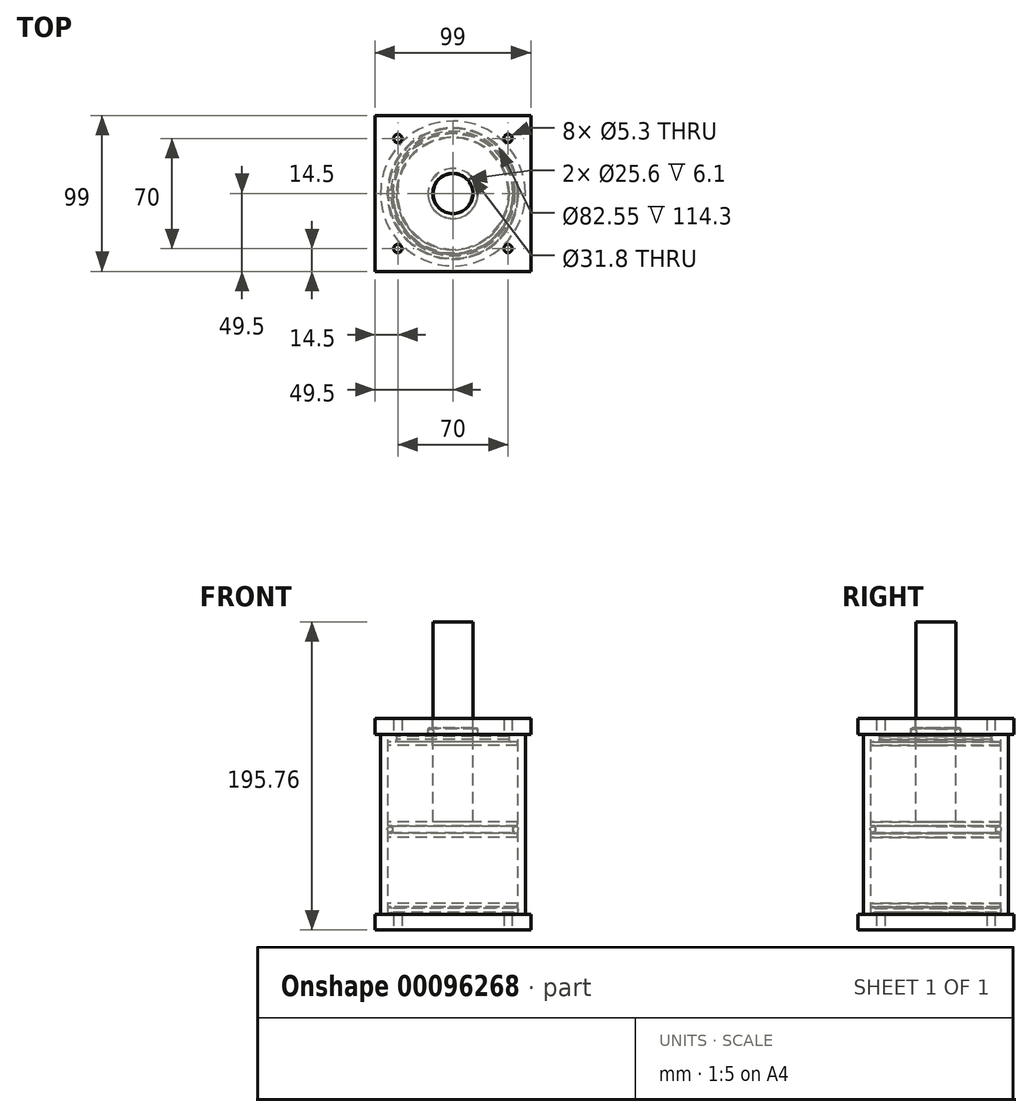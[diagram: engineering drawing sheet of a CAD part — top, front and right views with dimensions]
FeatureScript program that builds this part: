
annotation { "Feature Type Name" : "Feature", "Feature Type Description" : "" }
export const myFeature = defineFeature(function(context is Context, id is Id, definition is map)
    precondition{}
    {
        {
            var Q0;
            Q0=qCreatedBy(makeId("Front.planeOp"),FACE);
            var sketch = newSketch(context, id + "F0", { "sketchPlane" : qUnion([Q0])});
            skLineSegment(sketch, "E0", {"start": v(0, 90.15) * mm, "end": v(0, -78.3) * mm, "construction": true});
            skSolve(sketch);
        }
        {
            var Q0;
            Q0=qCreatedBy(makeId("Front.planeOp"),FACE);
            var sketch = newSketch(context, id + "F1", { "sketchPlane" : qUnion([Q0])});
            skLineSegment(sketch, "E1", {"start": v(0, 0) * mm, "end": v(12.7, 0) * mm});
            skLineSegment(sketch, "E2", {"start": v(12.7, 0) * mm, "end": v(12.7, 127) * mm});
            skLineSegment(sketch, "E3", {"start": v(12.7, 127) * mm, "end": v(0, 127) * mm});
            skLineSegment(sketch, "E4", {"start": v(0, 127) * mm, "end": v(0, 0) * mm});
            skSolve(sketch);
        }
        {
            var Q0;
            Q0=qCreatedBy(makeId("Front.planeOp"),FACE);
            var sketch = newSketch(context, id + "F2", { "sketchPlane" : qUnion([Q0])});
            skLineSegment(sketch, "E5", {"start": v(41.27, 55.54) * mm, "end": v(41.28, -58.76) * mm});
            skLineSegment(sketch, "E6", {"start": v(41.27, 55.54) * mm, "end": v(46.04, 55.54) * mm});
            skLineSegment(sketch, "E7", {"start": v(46.04, 55.54) * mm, "end": v(46.04, -58.76) * mm});
            skLineSegment(sketch, "E8", {"start": v(46.04, -58.76) * mm, "end": v(41.28, -58.76) * mm});
            skPoint(sketch, "E9.orphan", {"position": v(41.28, -58.76) * mm});
            skLineSegment(sketch, "E10", {"start": v(46.04, -1.61) * mm, "end": v(-49.68, -1.61) * mm, "construction": true});
            skSolve(sketch);
        }
        {
            var Q0;
            Q0=qCreatedBy(makeId("Front.planeOp"),FACE);
            var sketch = newSketch(context, id + "F3", { "sketchPlane" : qUnion([Q0])});
            skLineSegment(sketch, "E11", {"start": v(0, 0) * mm, "end": v(41.17, 0) * mm});
            skLineSegment(sketch, "E12", {"start": v(41.17, 0) * mm, "end": v(41.17, -2.6) * mm});
            skLineSegment(sketch, "E13", {"start": v(41.17, -2.6) * mm, "end": v(38.19, -2.6) * mm});
            skLineSegment(sketch, "E14", {"start": v(38.19, -2.6) * mm, "end": v(38.19, -7.4) * mm});
            skLineSegment(sketch, "E15", {"start": v(38.19, -7.4) * mm, "end": v(41.17, -7.4) * mm});
            skLineSegment(sketch, "E16", {"start": v(41.17, -7.4) * mm, "end": v(41.17, -10) * mm});
            skLineSegment(sketch, "E17", {"start": v(41.17, -10) * mm, "end": v(0, -10) * mm});
            skLineSegment(sketch, "E18", {"start": v(0, -10) * mm, "end": v(0, 0) * mm});
            skCircle(sketch, "E19", {"center": v(39.95, -4.9) * mm, "radius": 1.76 * mm});
            skSolve(sketch);
        }
        {
            var Q0;
            Q0=qCreatedBy(makeId("Front.planeOp"),FACE);
            var sketch = newSketch(context, id + "F4", { "sketchPlane" : qUnion([Q0])});
            skLineSegment(sketch, "E20", {"start": v(0, -51.76) * mm, "end": v(0, -68.76) * mm});
            skLineSegment(sketch, "E21", {"start": v(0, -68.76) * mm, "end": v(70, -68.76) * mm});
            skLineSegment(sketch, "E22", {"start": v(70, -68.76) * mm, "end": v(70, -58.76) * mm});
            skLineSegment(sketch, "E23", {"start": v(70, -58.76) * mm, "end": v(38.58, -58.76) * mm});
            skLineSegment(sketch, "E24", {"start": v(41.17, -53.96) * mm, "end": v(41.17, -51.76) * mm});
            skLineSegment(sketch, "E25.trimOffspring", {"start": v(41.17, -51.76) * mm, "end": v(0, -51.76) * mm});
            skCircle(sketch, "E26", {"center": v(39.92, -56.36) * mm, "radius": 1.77 * mm});
            skLineSegment(sketch, "E27", {"start": v(38.58, -58.76) * mm, "end": v(38.58, -53.96) * mm});
            skLineSegment(sketch, "E28", {"start": v(38.58, -53.96) * mm, "end": v(41.17, -53.96) * mm});
            skLineSegment(sketch, "E29.MirrorCS", {"start": v(35.85, 50.74) * mm, "end": v(41.17, 50.74) * mm});
            skLineSegment(sketch, "E30.MirrorCS", {"start": v(35.85, 55.54) * mm, "end": v(35.85, 50.74) * mm});
            skCircle(sketch, "E31.MirrorC", {"center": v(37.32, 53.26) * mm, "radius": 1.77 * mm});
            skLineSegment(sketch, "E32.MirrorCS", {"start": v(70, 65.54) * mm, "end": v(70, 55.54) * mm});
            skLineSegment(sketch, "E33.MirrorCS", {"start": v(41.17, 48.54) * mm, "end": v(12.8, 48.54) * mm});
            skLineSegment(sketch, "E34.MirrorCS", {"start": v(70, 55.54) * mm, "end": v(35.85, 55.54) * mm});
            skLineSegment(sketch, "E35.MirrorCS", {"start": v(41.17, 50.74) * mm, "end": v(41.17, 48.54) * mm});
            skLineSegment(sketch, "E36.MirrorCS", {"start": v(12.8, 65.54) * mm, "end": v(70, 65.54) * mm});
            skLineSegment(sketch, "E37", {"start": v(12.8, 48.54) * mm, "end": v(12.8, 54.64) * mm});
            skPoint(sketch, "E38", {"position": v(38.58, -56.36) * mm});
            skLineSegment(sketch, "E39", {"start": v(12.8, 54.64) * mm, "end": v(15.9, 54.64) * mm});
            skLineSegment(sketch, "E40", {"start": v(15.9, 54.64) * mm, "end": v(15.9, 59.44) * mm});
            skLineSegment(sketch, "E41", {"start": v(15.9, 59.44) * mm, "end": v(12.8, 59.44) * mm});
            skLineSegment(sketch, "E42.trimOffspring", {"start": v(12.8, 59.44) * mm, "end": v(12.8, 65.54) * mm});
            skCircle(sketch, "E43", {"center": v(14.07, 57.14) * mm, "radius": 1.76 * mm});
            skLineSegment(sketch, "E44", {"start": v(70, -58.76) * mm, "end": v(70, 76.42) * mm, "construction": true});
            skSolve(sketch);
        }
        {
            var Q0;
            Q0=makeQuery(id+"F3.imprint","IMPRINT",FACE,{"disambiguationData":[TD([[makeQuery(id+"F3.imprint","IMPRINT",EDGE,{"derivedFrom":sQuery(id+"F3.wireOp",EDGE,"E11")}),-1.0]])]});
            var Q1;
            Q1=makeQuery(id+"F3.imprint","IMPRINT",FACE,{"disambiguationData":[TD([[makeQuery(id+"F3.imprint","IMPRINT",EDGE,{"derivedFrom":sQuery(id+"F3.wireOp",EDGE,"E19")}),1.0]])]});
            var Q2;
            Q2=sQuery(id+"F0.wireOp",EDGE,"E0");
            revolve(context, id + "F5", {"entities" : qUnion([Q0, Q1]), "axis" : qUnion([Q2]), "revolveType" : RevolveType.FULL});
        }
        {
            var Q0;
            Q0=makeQuery(id+"F5.opRevolve","SWEPT_EDGE",EDGE,{"disambiguationData":[OSD([sQuery(id+"F3.wireOp",EDGE,"E14"),sQuery(id+"F3.wireOp",EDGE,"E15")])]});
            var Q1;
            Q1=makeQuery(id+"F5.opRevolve","SWEPT_EDGE",EDGE,{"disambiguationData":[OSD([sQuery(id+"F3.wireOp",EDGE,"E13"),sQuery(id+"F3.wireOp",EDGE,"E14")])]});
            fillet(context, id + "F6", {"entities" : qUnion([Q0, Q1]), "radius" : 1 * mm, "tangentPropagation" : true, "allowEdgeOverflow" : false});
        }
        {
            var Q0;
            Q0=makeQuery(id+"F4.imprint","IMPRINT",FACE,{"disambiguationData":[TD([[makeQuery(id+"F4.imprint","IMPRINT",EDGE,{"derivedFrom":sQuery(id+"F4.wireOp",EDGE,"E43")}),1.0]])]});
            var Q1;
            Q1=makeQuery(id+"F4.imprint","IMPRINT",FACE,{"disambiguationData":[TD([[makeQuery(id+"F4.imprint","IMPRINT",EDGE,{"derivedFrom":sQuery(id+"F4.wireOp",EDGE,"E31.MirrorC")}),-1.0]])]});
            var Q2;
            Q2=makeQuery(id+"F4.imprint","IMPRINT",FACE,{"disambiguationData":[TD([[makeQuery(id+"F4.imprint","IMPRINT",EDGE,{"derivedFrom":sQuery(id+"F4.wireOp",EDGE,"E29.MirrorCS")}),-1.0]])]});
            var Q3;
            Q3=sQuery(id+"F0.wireOp",EDGE,"E0");
            revolve(context, id + "F7", {"entities" : qUnion([Q0, Q1, Q2]), "axis" : qUnion([Q3]), "revolveType" : RevolveType.FULL});
        }
        {
            var Q0;
            Q0=makeQuery(id+"F7.opRevolve","SWEPT_EDGE",EDGE,{"disambiguationData":[OSD([sQuery(id+"F4.wireOp",EDGE,"E30.MirrorCS"),sQuery(id+"F4.wireOp",EDGE,"E34.MirrorCS")])]});
            var Q1;
            Q1=makeQuery(id+"F7.opRevolve","SWEPT_EDGE",EDGE,{"disambiguationData":[OSD([sQuery(id+"F4.wireOp",EDGE,"E29.MirrorCS"),sQuery(id+"F4.wireOp",EDGE,"E30.MirrorCS")])]});
            fillet(context, id + "F8", {"entities" : qUnion([Q0, Q1]), "radius" : 1 * mm, "tangentPropagation" : true, "allowEdgeOverflow" : false});
        }
        {
            var Q0;
            Q0=makeQuery(id+"F4.imprint","IMPRINT",FACE,{"disambiguationData":[TD([[makeQuery(id+"F4.imprint","IMPRINT",EDGE,{"derivedFrom":sQuery(id+"F4.wireOp",EDGE,"E26")}),1.0]])]});
            var Q1;
            Q1=makeQuery(id+"F4.imprint","IMPRINT",FACE,{"disambiguationData":[TD([[makeQuery(id+"F4.imprint","IMPRINT",EDGE,{"derivedFrom":sQuery(id+"F4.wireOp",EDGE,"E20")}),1.0]])]});
            var Q2;
            Q2=sQuery(id+"F0.wireOp",EDGE,"E0");
            revolve(context, id + "F9", {"entities" : qUnion([Q0, Q1]), "axis" : qUnion([Q2]), "revolveType" : RevolveType.FULL});
        }
        {
            var Q0;
            Q0=makeQuery(id+"F9.opRevolve","SWEPT_EDGE",EDGE,{"disambiguationData":[OSD([sQuery(id+"F4.wireOp",EDGE,"E27"),sQuery(id+"F4.wireOp",EDGE,"E28")])]});
            var Q1;
            Q1=makeQuery(id+"F9.opRevolve","SWEPT_EDGE",EDGE,{"disambiguationData":[OSD([sQuery(id+"F4.wireOp",EDGE,"E23"),sQuery(id+"F4.wireOp",EDGE,"E27")])]});
            chamfer(context, id + "F10", {"entities" : qUnion([Q0, Q1]), "width" : 1 * mm, "tangentPropagation" : true});
        }
        {
            var Q0;
            Q0=makeQuery(id+"F1.imprint","IMPRINT",FACE,{"disambiguationData":[TD([[makeQuery(id+"F1.imprint","IMPRINT",EDGE,{"derivedFrom":sQuery(id+"F1.wireOp",EDGE,"E1")}),1.0]])]});
            var Q1;
            Q1=sQuery(id+"F0.wireOp",EDGE,"E0");
            revolve(context, id + "F11", {"entities" : qUnion([Q0]), "axis" : qUnion([Q1]), "revolveType" : RevolveType.FULL});
        }
        {
            var Q0;
            Q0=makeQuery(id+"F7.opRevolve","SWEPT_EDGE",EDGE,{"disambiguationData":[OSD([sQuery(id+"F4.wireOp",EDGE,"E40"),sQuery(id+"F4.wireOp",EDGE,"E41")])]});
            var Q1;
            Q1=makeQuery(id+"F7.opRevolve","SWEPT_EDGE",EDGE,{"disambiguationData":[OSD([sQuery(id+"F4.wireOp",EDGE,"E39"),sQuery(id+"F4.wireOp",EDGE,"E40")])]});
            fillet(context, id + "F12", {"entities" : qUnion([Q0, Q1]), "radius" : 1 * mm, "tangentPropagation" : true, "allowEdgeOverflow" : false});
        }
        {
            var Q0;
            Q0=makeQuery(id+"F2.imprint","IMPRINT",FACE,{"disambiguationData":[TD([[makeQuery(id+"F2.imprint","IMPRINT",EDGE,{"derivedFrom":sQuery(id+"F2.wireOp",EDGE,"E5")}),1.0]])]});
            var Q1;
            Q1=sQuery(id+"F0.wireOp",EDGE,"E0");
            revolve(context, id + "F13", {"entities" : qUnion([Q0]), "axis" : qUnion([Q1]), "revolveType" : RevolveType.FULL});
        }
        {
            var Q0;
            Q0=makeQuery(id+"F9.opRevolve","SWEPT_FACE",FACE,{"disambiguationData":[OSD([sQuery(id+"F4.wireOp",EDGE,"E21")])]});
            var sketch = newSketch(context, id + "F14", { "sketchPlane" : qUnion([Q0])});
            skLineSegment(sketch, "E45.bottom", {"start": v(49.5, 49.5) * mm, "end": v(-49.5, 49.5) * mm});
            skLineSegment(sketch, "E45.top", {"start": v(49.5, -49.5) * mm, "end": v(-49.5, -49.5) * mm});
            skLineSegment(sketch, "E45.left", {"start": v(49.5, 49.5) * mm, "end": v(49.5, -49.5) * mm});
            skLineSegment(sketch, "E45.right", {"start": v(-49.5, 49.5) * mm, "end": v(-49.5, -49.5) * mm});
            skPoint(sketch, "E45.middle", {"position": v(0, 0) * mm});
            skSolve(sketch);
        }
        {
            var Q0;
            {var subQ0=sQuery(id+"F14.wireOp",EDGE,"E45.bottom");Q0=makeQuery(id+"F14.imprint","IMPRINT",FACE,{"disambiguationData":[TD([[makeQuery(id+"F14.imprint","IMPRINT",EDGE,{"derivedFrom":subQ0}),-1.0]])]});}
            var Q1;
            {var subQ0=sQuery(id+"F14.wireOp",EDGE,"E45.right");Q1=makeQuery(id+"F14.imprint","IMPRINT",FACE,{"disambiguationData":[TD([[makeQuery(id+"F14.imprint","IMPRINT",EDGE,{"derivedFrom":subQ0}),-1.0]])]});}
            var Q2;
            {var subQ0=sQuery(id+"F14.wireOp",EDGE,"E45.left");Q2=makeQuery(id+"F14.imprint","IMPRINT",FACE,{"disambiguationData":[TD([[makeQuery(id+"F14.imprint","IMPRINT",EDGE,{"derivedFrom":subQ0}),1.0]])]});}
            var Q3;
            {var subQ0=sQuery(id+"F14.wireOp",EDGE,"E45.top");Q3=makeQuery(id+"F14.imprint","IMPRINT",FACE,{"disambiguationData":[TD([[makeQuery(id+"F14.imprint","IMPRINT",EDGE,{"derivedFrom":subQ0}),1.0]])]});}
            extrude(context, id + "F15", {"entities" : qUnion([Q0, Q1, Q2, Q3]), "operationType" : NewBodyOperationType.REMOVE, "endBound" : BoundingType.THROUGH_ALL, "oppositeDirection" : true, "depth" : 25 * mm});
        }
        {
            var Q0;
            Q0=makeQuery(id+"F9.opRevolve","SWEPT_FACE",FACE,{"disambiguationData":[OSD([sQuery(id+"F4.wireOp",EDGE,"E21")])]});
            var sketch = newSketch(context, id + "F16", { "sketchPlane" : qUnion([Q0])});
            skPoint(sketch, "E46", {"position": v(-35, 35) * mm});
            skPoint(sketch, "E47.0.1.0", {"position": v(-35, -35) * mm});
            skPoint(sketch, "E47.1.0.0", {"position": v(35, 35) * mm});
            skPoint(sketch, "E47.1.1.0", {"position": v(35, -35) * mm});
            skLineSegment(sketch, "E47.direction1", {"start": v(-35, 35) * mm, "end": v(35, 35) * mm, "construction": true});
            skLineSegment(sketch, "E47.direction2", {"start": v(-35, 35) * mm, "end": v(-35, -35) * mm, "construction": true});
            skSolve(sketch);
        }
        {
            var Q0;
            Q0=sQuery(id+"F16.wireOp",VERTEX,"E46");
            var Q1;
            Q1=sQuery(id+"F16.wireOp",VERTEX,"E47.1.0.0");
            var Q2;
            Q2=sQuery(id+"F16.wireOp",VERTEX,"E47.1.1.0");
            var Q3;
            Q3=sQuery(id+"F16.wireOp",VERTEX,"E47.0.1.0");
            var Q4;
            Q4=makeQuery(id+"F9.opRevolve","SWEPT_BODY",BODY,{"disambiguationData":[OSD([sQuery(id+"F4.wireOp",EDGE,"E20"),sQuery(id+"F4.wireOp",EDGE,"E21"),sQuery(id+"F4.wireOp",EDGE,"E22"),sQuery(id+"F4.wireOp",EDGE,"E23"),sQuery(id+"F4.wireOp",EDGE,"E24"),sQuery(id+"F4.wireOp",EDGE,"E25.trimOffspring"),sQuery(id+"F4.wireOp",EDGE,"E27"),sQuery(id+"F4.wireOp",EDGE,"E28")])]});
            var Q5;
            Q5=makeQuery(id+"F7.opRevolve","SWEPT_BODY",BODY,{"disambiguationData":[OSD([sQuery(id+"F4.wireOp",EDGE,"E29.MirrorCS"),sQuery(id+"F4.wireOp",EDGE,"E30.MirrorCS"),sQuery(id+"F4.wireOp",EDGE,"E32.MirrorCS"),sQuery(id+"F4.wireOp",EDGE,"E33.MirrorCS"),sQuery(id+"F4.wireOp",EDGE,"E34.MirrorCS"),sQuery(id+"F4.wireOp",EDGE,"E35.MirrorCS"),sQuery(id+"F4.wireOp",EDGE,"E36.MirrorCS"),sQuery(id+"F4.wireOp",EDGE,"E37"),sQuery(id+"F4.wireOp",EDGE,"E39"),sQuery(id+"F4.wireOp",EDGE,"E40"),sQuery(id+"F4.wireOp",EDGE,"E41"),sQuery(id+"F4.wireOp",EDGE,"E42.trimOffspring")])]});
            hole(context, id + "F17", {"style" : HoleStyle.SIMPLE, "endStyle" : HoleEndStyle.THROUGH, "holeDiameter" : 5.3 * mm, "locations" : qUnion([Q0, Q1, Q2, Q3]), "scope" : qUnion([Q4, Q5]), "isTappedThrough" : true});
        }
    });
